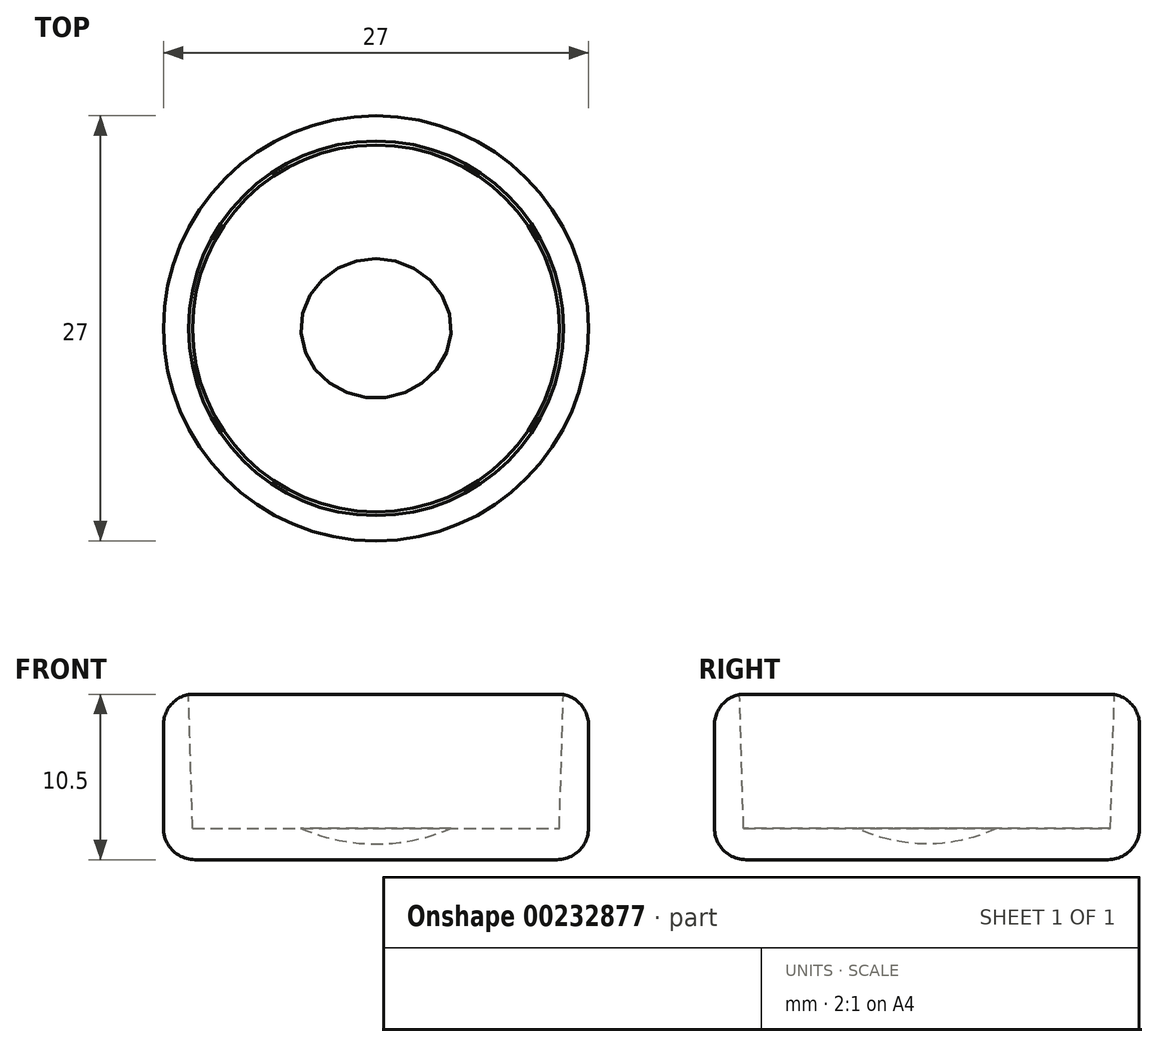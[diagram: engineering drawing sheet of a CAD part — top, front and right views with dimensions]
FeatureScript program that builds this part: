
annotation { "Feature Type Name" : "Feature", "Feature Type Description" : "" }
export const myFeature = defineFeature(function(context is Context, id is Id, definition is map)
    precondition{}
    {
        {
            var Q0;
            Q0=qCreatedBy(makeId("Front.planeOp"),FACE);
            var sketch = newSketch(context, id + "F0", { "sketchPlane" : qUnion([Q0])});
            skLineSegment(sketch, "E0.bottom", {"start": v(0, 0) * mm, "end": v(-13.5, 0) * mm});
            skLineSegment(sketch, "E0.top", {"start": v(0, 2) * mm, "end": v(-13.5, 2) * mm});
            skLineSegment(sketch, "E0.left", {"start": v(0, 0) * mm, "end": v(0, 2) * mm});
            skLineSegment(sketch, "E0.right", {"start": v(-13.5, 0) * mm, "end": v(-13.5, 2) * mm});
            skLineSegment(sketch, "E1", {"start": v(-13.5, 2) * mm, "end": v(-13.5, 10.5) * mm});
            skLineSegment(sketch, "E2", {"start": v(-11.9, 10.5) * mm, "end": v(-11.65, 2) * mm});
            skLineSegment(sketch, "E3", {"start": v(-13.5, 10.5) * mm, "end": v(-11.9, 10.5) * mm});
            skSolve(sketch);
        }
        {
            var Q0;
            Q0 = qSketchRegion(id + "F0", true);
            var Q1;
            Q1=sQuery(id+"F0.wireOp",EDGE,"E0.left");
            revolve(context, id + "F1", {"entities" : qUnion([Q0]), "axis" : qUnion([Q1]), "revolveType" : RevolveType.FULL});
        }
        {
            var Q0;
            Q0=makeQuery(id+"F1.opRevolve","SWEPT_EDGE",EDGE,{"disambiguationData":[OSD([sQuery(id+"F0.wireOp",EDGE,"E1"),sQuery(id+"F0.wireOp",EDGE,"E3")])]});
            var Q1;
            Q1=makeQuery(id+"F1.opRevolve","SWEPT_EDGE",EDGE,{"disambiguationData":[OSD([sQuery(id+"F0.wireOp",EDGE,"E0.bottom"),sQuery(id+"F0.wireOp",EDGE,"E0.right")])]});
            fillet(context, id + "F2", {"entities" : qUnion([Q0, Q1]), "radius" : 2 * mm, "tangentPropagation" : true, "allowEdgeOverflow" : false});
        }
        {
            var Q0;
            Q0=qCreatedBy(makeId("Front.planeOp"),FACE);
            var sketch = newSketch(context, id + "F3", { "sketchPlane" : qUnion([Q0])});
            skArc(sketch, "E4", {"start": v(-11.8, 11.4) * mm, "mid": v(-0.1, 1) * mm, "end": v(11.78, 11.2) * mm});
            skLineSegment(sketch, "E5", {"start": v(-11.8, 11.4) * mm, "end": v(11.78, 11.2) * mm});
            skSolve(sketch);
        }
        {
            var Q0;
            Q0=makeQuery(id+"F3.imprint","IMPRINT",FACE,{"disambiguationData":[TD([[makeQuery(id+"F3.imprint","IMPRINT",EDGE,{"derivedFrom":sQuery(id+"F3.wireOp",EDGE,"E4")}),1.0]])]});
            var Q1;
            Q1=sQuery(id+"F3.wireOp",EDGE,"E5");
            revolve(context, id + "F4", {"operationType" : NewBodyOperationType.REMOVE, "entities" : qUnion([Q0]), "axis" : qUnion([Q1]), "revolveType" : RevolveType.FULL, "oppositeDirection" : true});
        }
    });
